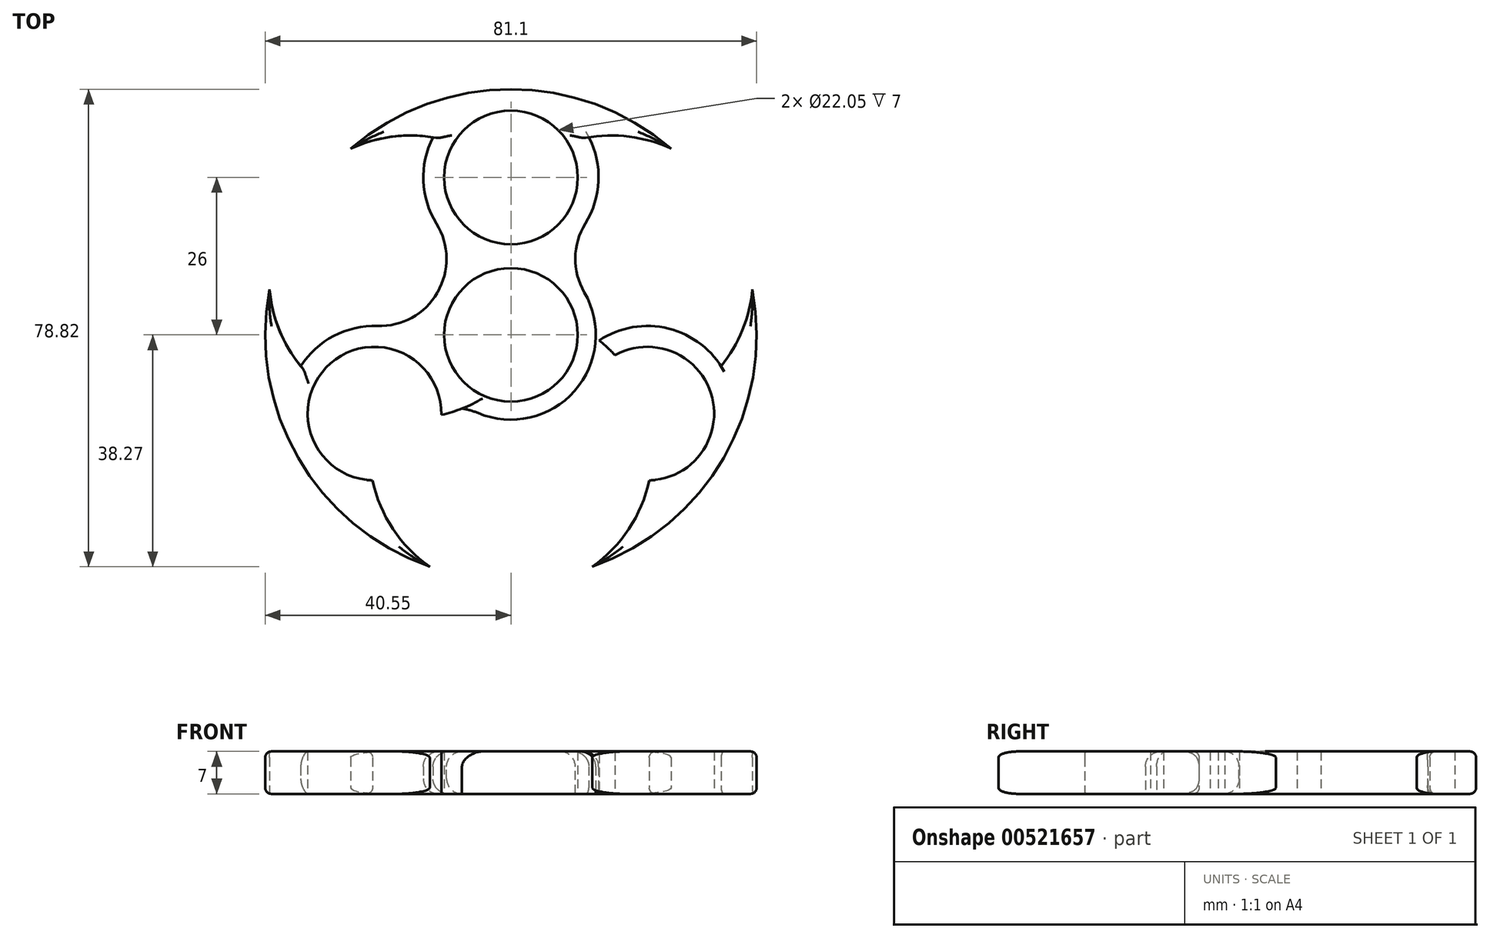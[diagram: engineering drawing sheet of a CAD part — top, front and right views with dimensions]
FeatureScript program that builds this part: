
annotation { "Feature Type Name" : "Feature", "Feature Type Description" : "" }
export const myFeature = defineFeature(function(context is Context, id is Id, definition is map)
    precondition{}
    {
        {
            var Q0;
            Q0=qCreatedBy(makeId("Top.planeOp"),FACE);
            var sketch = newSketch(context, id + "F0", { "sketchPlane" : qUnion([Q0])});
            skCircle(sketch, "E0", {"center": v(0, 0) * mm, "radius": 11.03 * mm});
            skCircle(sketch, "E1", {"center": v(0, 26) * mm, "radius": 11.03 * mm});
            skCircle(sketch, "E2.1.0", {"center": v(-22.52, -13) * mm, "radius": 11.03 * mm});
            skCircle(sketch, "E2.2.0", {"center": v(22.52, -13) * mm, "radius": 11.03 * mm});
            skCircle(sketch, "E3", {"center": v(0, 0) * mm, "radius": 40.55 * mm});
            skCircle(sketch, "E4", {"center": v(0, 0) * mm, "radius": 37 * mm});
            skCircle(sketch, "E5", {"center": v(0, 26) * mm, "radius": 14.47 * mm});
            skCircle(sketch, "E6.1.0", {"center": v(-22.52, -13) * mm, "radius": 14.47 * mm});
            skCircle(sketch, "E6.2.0", {"center": v(22.52, -13) * mm, "radius": 14.47 * mm});
            skLineSegment(sketch, "E7", {"start": v(-22.52, -13) * mm, "end": v(0, 26) * mm, "construction": true});
            skLineSegment(sketch, "E8", {"start": v(0, 26) * mm, "end": v(22.52, -13) * mm, "construction": true});
            skLineSegment(sketch, "E9", {"start": v(-22.52, -13) * mm, "end": v(22.52, -13) * mm, "construction": true});
            skPoint(sketch, "E10.endSnap0", {"position": v(0, -13) * mm});
            skCircle(sketch, "E11", {"center": v(0, 0) * mm, "radius": 42.5 * mm, "construction": true});
            skLineSegment(sketch, "E12", {"start": v(-11.26, 6.5) * mm, "end": v(-36.8, 21.25) * mm, "construction": true});
            skLineSegment(sketch, "E13", {"start": v(11.26, 6.5) * mm, "end": v(36.8, 21.25) * mm, "construction": true});
            skLineSegment(sketch, "E14", {"start": v(0, -13) * mm, "end": v(0, -42.5) * mm, "construction": true});
            skCircle(sketch, "E15", {"center": v(-16.6, 9.58) * mm, "radius": 23.34 * mm});
            skCircle(sketch, "E16", {"center": v(16.6, 9.58) * mm, "radius": 23.34 * mm});
            skCircle(sketch, "E17", {"center": v(0, -19.16) * mm, "radius": 23.34 * mm});
            skCircle(sketch, "E18", {"center": v(0, 0) * mm, "radius": 14 * mm});
            skSolve(sketch);
        }
        {
            var Q0;
            {var subQ6=sQuery(id+"F0.wireOp",EDGE,"E3");var subQ8=sQuery(id+"F0.wireOp",EDGE,"E16");var subQ10=makeQuery(id+"F0.imprint","INTERSECT",VERTEX,{"disambiguationData":[OD(0.0)],"derivedFrom":[subQ6,subQ8]});Q0=makeQuery(id+"F0.imprint","IMPRINT",FACE,{"disambiguationData":[TD([[makeQuery(id+"F0.imprint","IMPRINT",EDGE,{"disambiguationData":[TD([[subQ10,-1.0]])],"derivedFrom":subQ6}),1.0]])]});}
            var Q1;
            {var subQ0=sQuery(id+"F0.wireOp",EDGE,"E4");var subQ1=sQuery(id+"F0.wireOp",EDGE,"E1");var subQ2=makeQuery(id+"F0.imprint","INTERSECT",VERTEX,{"disambiguationData":[OD(0.0)],"derivedFrom":[subQ1,subQ0]});Q1=makeQuery(id+"F0.imprint","IMPRINT",FACE,{"disambiguationData":[TD([[makeQuery(id+"F0.imprint","IMPRINT",EDGE,{"disambiguationData":[TD([[subQ2,-1.0]])],"derivedFrom":subQ1}),-1.0]])]});}
            var Q2;
            {var subQ0=sQuery(id+"F0.wireOp",EDGE,"E5");var subQ1=sQuery(id+"F0.wireOp",EDGE,"E4");var subQ2=makeQuery(id+"F0.imprint","INTERSECT",VERTEX,{"disambiguationData":[OD(1.0)],"derivedFrom":[subQ1,subQ0]});Q2=makeQuery(id+"F0.imprint","IMPRINT",FACE,{"disambiguationData":[TD([[makeQuery(id+"F0.imprint","IMPRINT",EDGE,{"disambiguationData":[TD([[subQ2,-1.0]])],"derivedFrom":subQ1}),1.0]])]});}
            var Q3;
            {var subQ0=sQuery(id+"F0.wireOp",EDGE,"E4");var subQ1=sQuery(id+"F0.wireOp",EDGE,"E1");var subQ2=makeQuery(id+"F0.imprint","INTERSECT",VERTEX,{"disambiguationData":[OD(1.0)],"derivedFrom":[subQ1,subQ0]});Q3=makeQuery(id+"F0.imprint","IMPRINT",FACE,{"disambiguationData":[TD([[makeQuery(id+"F0.imprint","IMPRINT",EDGE,{"disambiguationData":[TD([[subQ2,-1.0]])],"derivedFrom":subQ1}),-1.0]])]});}
            var Q4;
            {var subQ0=sQuery(id+"F0.wireOp",EDGE,"E15");var subQ1=sQuery(id+"F0.wireOp",EDGE,"E1");var subQ2=makeQuery(id+"F0.imprint","INTERSECT",VERTEX,{"disambiguationData":[OD(0.0)],"derivedFrom":[subQ1,subQ0]});Q4=makeQuery(id+"F0.imprint","IMPRINT",FACE,{"disambiguationData":[TD([[makeQuery(id+"F0.imprint","IMPRINT",EDGE,{"disambiguationData":[TD([[subQ2,-1.0]])],"derivedFrom":subQ1}),-1.0]])]});}
            var Q5;
            {var subQ0=sQuery(id+"F0.wireOp",EDGE,"E4");var subQ1=sQuery(id+"F0.wireOp",EDGE,"E1");var subQ2=makeQuery(id+"F0.imprint","INTERSECT",VERTEX,{"disambiguationData":[OD(0.0)],"derivedFrom":[subQ1,subQ0]});Q5=makeQuery(id+"F0.imprint","IMPRINT",FACE,{"disambiguationData":[TD([[makeQuery(id+"F0.imprint","IMPRINT",EDGE,{"disambiguationData":[TD([[subQ2,1.0]])],"derivedFrom":subQ1}),-1.0]])]});}
            var Q6;
            {var subQ0=sQuery(id+"F0.wireOp",EDGE,"E5");var subQ1=sQuery(id+"F0.wireOp",EDGE,"E4");var subQ2=makeQuery(id+"F0.imprint","INTERSECT",VERTEX,{"disambiguationData":[OD(0.0)],"derivedFrom":[subQ1,subQ0]});Q6=makeQuery(id+"F0.imprint","IMPRINT",FACE,{"disambiguationData":[TD([[makeQuery(id+"F0.imprint","IMPRINT",EDGE,{"disambiguationData":[TD([[subQ2,1.0]])],"derivedFrom":subQ1}),1.0]])]});}
            var Q7;
            {var subQ0=sQuery(id+"F0.wireOp",EDGE,"E16");var subQ1=sQuery(id+"F0.wireOp",EDGE,"E1");var subQ2=makeQuery(id+"F0.imprint","INTERSECT",VERTEX,{"disambiguationData":[OD(0.0)],"derivedFrom":[subQ1,subQ0]});Q7=makeQuery(id+"F0.imprint","IMPRINT",FACE,{"disambiguationData":[TD([[makeQuery(id+"F0.imprint","IMPRINT",EDGE,{"disambiguationData":[TD([[subQ2,1.0]])],"derivedFrom":subQ1}),-1.0]])]});}
            var Q8;
            {var subQ0=sQuery(id+"F0.wireOp",EDGE,"E16");var subQ1=sQuery(id+"F0.wireOp",EDGE,"E2.2.0");var subQ2=makeQuery(id+"F0.imprint","INTERSECT",VERTEX,{"disambiguationData":[OD(0.0)],"derivedFrom":[subQ1,subQ0]});Q8=makeQuery(id+"F0.imprint","IMPRINT",FACE,{"disambiguationData":[TD([[makeQuery(id+"F0.imprint","IMPRINT",EDGE,{"disambiguationData":[TD([[subQ2,-1.0]])],"derivedFrom":subQ1}),-1.0]])]});}
            var Q9;
            {var subQ0=sQuery(id+"F0.wireOp",EDGE,"E4");var subQ1=sQuery(id+"F0.wireOp",EDGE,"E2.2.0");var subQ2=makeQuery(id+"F0.imprint","INTERSECT",VERTEX,{"disambiguationData":[OD(1.0)],"derivedFrom":[subQ1,subQ0]});Q9=makeQuery(id+"F0.imprint","IMPRINT",FACE,{"disambiguationData":[TD([[makeQuery(id+"F0.imprint","IMPRINT",EDGE,{"disambiguationData":[TD([[subQ2,-1.0]])],"derivedFrom":subQ1}),-1.0]])]});}
            var Q10;
            {var subQ0=sQuery(id+"F0.wireOp",EDGE,"E4");var subQ1=sQuery(id+"F0.wireOp",EDGE,"E2.2.0");var subQ2=makeQuery(id+"F0.imprint","INTERSECT",VERTEX,{"disambiguationData":[OD(0.0)],"derivedFrom":[subQ1,subQ0]});Q10=makeQuery(id+"F0.imprint","IMPRINT",FACE,{"disambiguationData":[TD([[makeQuery(id+"F0.imprint","IMPRINT",EDGE,{"disambiguationData":[TD([[subQ2,-1.0]])],"derivedFrom":subQ1}),-1.0]])]});}
            var Q11;
            {var subQ4=sQuery(id+"F0.wireOp",EDGE,"E16");var subQ8=sQuery(id+"F0.wireOp",EDGE,"E3");var subQ9=makeQuery(id+"F0.imprint","INTERSECT",VERTEX,{"disambiguationData":[OD(1.0)],"derivedFrom":[subQ8,subQ4]});Q11=makeQuery(id+"F0.imprint","IMPRINT",FACE,{"disambiguationData":[TD([[makeQuery(id+"F0.imprint","IMPRINT",EDGE,{"disambiguationData":[TD([[subQ9,1.0]])],"derivedFrom":subQ8}),1.0]])]});}
            var Q12;
            {var subQ0=sQuery(id+"F0.wireOp",EDGE,"E6.2.0");var subQ1=sQuery(id+"F0.wireOp",EDGE,"E4");var subQ2=makeQuery(id+"F0.imprint","INTERSECT",VERTEX,{"disambiguationData":[OD(1.0)],"derivedFrom":[subQ1,subQ0]});Q12=makeQuery(id+"F0.imprint","IMPRINT",FACE,{"disambiguationData":[TD([[makeQuery(id+"F0.imprint","IMPRINT",EDGE,{"disambiguationData":[TD([[subQ2,-1.0]])],"derivedFrom":subQ1}),1.0]])]});}
            var Q13;
            {var subQ0=sQuery(id+"F0.wireOp",EDGE,"E17");var subQ1=sQuery(id+"F0.wireOp",EDGE,"E4");var subQ2=makeQuery(id+"F0.imprint","INTERSECT",VERTEX,{"disambiguationData":[OD(1.0)],"derivedFrom":[subQ1,subQ0]});Q13=makeQuery(id+"F0.imprint","IMPRINT",FACE,{"disambiguationData":[TD([[makeQuery(id+"F0.imprint","IMPRINT",EDGE,{"disambiguationData":[TD([[subQ2,-1.0]])],"derivedFrom":subQ1}),1.0]])]});}
            var Q14;
            {var subQ5=sQuery(id+"F0.wireOp",EDGE,"E15");var subQ8=sQuery(id+"F0.wireOp",EDGE,"E3");var subQ9=makeQuery(id+"F0.imprint","INTERSECT",VERTEX,{"disambiguationData":[OD(1.0)],"derivedFrom":[subQ8,subQ5]});Q14=makeQuery(id+"F0.imprint","IMPRINT",FACE,{"disambiguationData":[TD([[makeQuery(id+"F0.imprint","IMPRINT",EDGE,{"disambiguationData":[TD([[subQ9,-1.0]])],"derivedFrom":subQ8}),1.0]])]});}
            var Q15;
            {var subQ0=sQuery(id+"F0.wireOp",EDGE,"E4");var subQ1=sQuery(id+"F0.wireOp",EDGE,"E2.1.0");var subQ2=makeQuery(id+"F0.imprint","INTERSECT",VERTEX,{"disambiguationData":[OD(0.0)],"derivedFrom":[subQ1,subQ0]});Q15=makeQuery(id+"F0.imprint","IMPRINT",FACE,{"disambiguationData":[TD([[makeQuery(id+"F0.imprint","IMPRINT",EDGE,{"disambiguationData":[TD([[subQ2,-1.0]])],"derivedFrom":subQ1}),-1.0]])]});}
            var Q16;
            {var subQ0=sQuery(id+"F0.wireOp",EDGE,"E15");var subQ1=sQuery(id+"F0.wireOp",EDGE,"E4");var subQ2=makeQuery(id+"F0.imprint","INTERSECT",VERTEX,{"disambiguationData":[OD(1.0)],"derivedFrom":[subQ1,subQ0]});Q16=makeQuery(id+"F0.imprint","IMPRINT",FACE,{"disambiguationData":[TD([[makeQuery(id+"F0.imprint","IMPRINT",EDGE,{"disambiguationData":[TD([[subQ2,-1.0]])],"derivedFrom":subQ1}),1.0]])]});}
            var Q17;
            {var subQ0=sQuery(id+"F0.wireOp",EDGE,"E4");var subQ1=sQuery(id+"F0.wireOp",EDGE,"E2.1.0");var subQ2=makeQuery(id+"F0.imprint","INTERSECT",VERTEX,{"disambiguationData":[OD(0.0)],"derivedFrom":[subQ1,subQ0]});Q17=makeQuery(id+"F0.imprint","IMPRINT",FACE,{"disambiguationData":[TD([[makeQuery(id+"F0.imprint","IMPRINT",EDGE,{"disambiguationData":[TD([[subQ2,1.0]])],"derivedFrom":subQ1}),-1.0]])]});}
            var Q18;
            {var subQ0=sQuery(id+"F0.wireOp",EDGE,"E4");var subQ1=sQuery(id+"F0.wireOp",EDGE,"E2.1.0");var subQ2=makeQuery(id+"F0.imprint","INTERSECT",VERTEX,{"disambiguationData":[OD(1.0)],"derivedFrom":[subQ1,subQ0]});Q18=makeQuery(id+"F0.imprint","IMPRINT",FACE,{"disambiguationData":[TD([[makeQuery(id+"F0.imprint","IMPRINT",EDGE,{"disambiguationData":[TD([[subQ2,-1.0]])],"derivedFrom":subQ1}),-1.0]])]});}
            var Q19;
            {var subQ0=sQuery(id+"F0.wireOp",EDGE,"E6.1.0");var subQ1=sQuery(id+"F0.wireOp",EDGE,"E4");var subQ2=makeQuery(id+"F0.imprint","INTERSECT",VERTEX,{"disambiguationData":[OD(1.0)],"derivedFrom":[subQ1,subQ0]});Q19=makeQuery(id+"F0.imprint","IMPRINT",FACE,{"disambiguationData":[TD([[makeQuery(id+"F0.imprint","IMPRINT",EDGE,{"disambiguationData":[TD([[subQ2,-1.0]])],"derivedFrom":subQ1}),1.0]])]});}
            var Q20;
            {var subQ0=sQuery(id+"F0.wireOp",EDGE,"E17");var subQ1=sQuery(id+"F0.wireOp",EDGE,"E2.1.0");var subQ2=makeQuery(id+"F0.imprint","INTERSECT",VERTEX,{"disambiguationData":[OD(0.0)],"derivedFrom":[subQ1,subQ0]});Q20=makeQuery(id+"F0.imprint","IMPRINT",FACE,{"disambiguationData":[TD([[makeQuery(id+"F0.imprint","IMPRINT",EDGE,{"disambiguationData":[TD([[subQ2,-1.0]])],"derivedFrom":subQ1}),-1.0]])]});}
            var Q21;
            {var subQ0=sQuery(id+"F0.wireOp",EDGE,"E15");var subQ1=sQuery(id+"F0.wireOp",EDGE,"E2.1.0");var subQ2=makeQuery(id+"F0.imprint","INTERSECT",VERTEX,{"disambiguationData":[OD(0.0)],"derivedFrom":[subQ1,subQ0]});Q21=makeQuery(id+"F0.imprint","IMPRINT",FACE,{"disambiguationData":[TD([[makeQuery(id+"F0.imprint","IMPRINT",EDGE,{"disambiguationData":[TD([[subQ2,1.0]])],"derivedFrom":subQ1}),-1.0]])]});}
            var Q22;
            {var subQ0=sQuery(id+"F0.wireOp",EDGE,"E16");var subQ1=sQuery(id+"F0.wireOp",EDGE,"E0");var subQ2=makeQuery(id+"F0.imprint","INTERSECT",VERTEX,{"disambiguationData":[OD(0.0)],"derivedFrom":[subQ1,subQ0]});Q22=makeQuery(id+"F0.imprint","IMPRINT",FACE,{"disambiguationData":[TD([[makeQuery(id+"F0.imprint","IMPRINT",EDGE,{"disambiguationData":[TD([[subQ2,-1.0]])],"derivedFrom":subQ1}),-1.0]])]});}
            var Q23;
            {var subQ1=sQuery(id+"F0.wireOp",EDGE,"E1");var subQ7=sQuery(id+"F0.wireOp",EDGE,"E16");var subQ8=makeQuery(id+"F0.imprint","INTERSECT",VERTEX,{"disambiguationData":[OD(1.0)],"derivedFrom":[subQ1,subQ7]});Q23=makeQuery(id+"F0.imprint","IMPRINT",FACE,{"disambiguationData":[TD([[makeQuery(id+"F0.imprint","IMPRINT",EDGE,{"disambiguationData":[TD([[subQ8,-1.0]])],"derivedFrom":subQ1}),-1.0]])]});}
            var Q24;
            {var subQ0=sQuery(id+"F0.wireOp",EDGE,"E18");var subQ1=sQuery(id+"F0.wireOp",EDGE,"E5");var subQ2=makeQuery(id+"F0.imprint","INTERSECT",VERTEX,{"disambiguationData":[OD(0.0)],"derivedFrom":[subQ1,subQ0]});Q24=makeQuery(id+"F0.imprint","IMPRINT",FACE,{"disambiguationData":[TD([[makeQuery(id+"F0.imprint","IMPRINT",EDGE,{"disambiguationData":[TD([[subQ2,-1.0]])],"derivedFrom":subQ1}),1.0]])]});}
            var Q25;
            {var subQ1=sQuery(id+"F0.wireOp",EDGE,"E0");var subQ7=sQuery(id+"F0.wireOp",EDGE,"E15");var subQ10=makeQuery(id+"F0.imprint","INTERSECT",VERTEX,{"disambiguationData":[OD(0.0)],"derivedFrom":[subQ1,subQ7]});Q25=makeQuery(id+"F0.imprint","IMPRINT",FACE,{"disambiguationData":[TD([[makeQuery(id+"F0.imprint","IMPRINT",EDGE,{"disambiguationData":[TD([[subQ10,-1.0]])],"derivedFrom":subQ1}),-1.0]])]});}
            var Q26;
            {var subQ0=sQuery(id+"F0.wireOp",EDGE,"E15");var subQ1=sQuery(id+"F0.wireOp",EDGE,"E0");var subQ2=makeQuery(id+"F0.imprint","INTERSECT",VERTEX,{"disambiguationData":[OD(0.0)],"derivedFrom":[subQ1,subQ0]});Q26=makeQuery(id+"F0.imprint","IMPRINT",FACE,{"disambiguationData":[TD([[makeQuery(id+"F0.imprint","IMPRINT",EDGE,{"disambiguationData":[TD([[subQ2,1.0]])],"derivedFrom":subQ1}),-1.0]])]});}
            var Q27;
            {var subQ1=sQuery(id+"F0.wireOp",EDGE,"E0");var subQ8=sQuery(id+"F0.wireOp",EDGE,"E17");var subQ9=makeQuery(id+"F0.imprint","INTERSECT",VERTEX,{"disambiguationData":[OD(0.0)],"derivedFrom":[subQ1,subQ8]});Q27=makeQuery(id+"F0.imprint","IMPRINT",FACE,{"disambiguationData":[TD([[makeQuery(id+"F0.imprint","IMPRINT",EDGE,{"disambiguationData":[TD([[subQ9,1.0]])],"derivedFrom":subQ1}),-1.0]])]});}
            var Q28;
            {var subQ0=sQuery(id+"F0.wireOp",EDGE,"E18");var subQ1=sQuery(id+"F0.wireOp",EDGE,"E6.2.0");var subQ2=makeQuery(id+"F0.imprint","INTERSECT",VERTEX,{"disambiguationData":[OD(0.0)],"derivedFrom":[subQ1,subQ0]});Q28=makeQuery(id+"F0.imprint","IMPRINT",FACE,{"disambiguationData":[TD([[makeQuery(id+"F0.imprint","IMPRINT",EDGE,{"disambiguationData":[TD([[subQ2,-1.0]])],"derivedFrom":subQ1}),1.0]])]});}
            var Q29;
            {var subQ1=sQuery(id+"F0.wireOp",EDGE,"E2.2.0");var subQ7=sQuery(id+"F0.wireOp",EDGE,"E17");var subQ10=makeQuery(id+"F0.imprint","INTERSECT",VERTEX,{"disambiguationData":[OD(1.0)],"derivedFrom":[subQ1,subQ7]});Q29=makeQuery(id+"F0.imprint","IMPRINT",FACE,{"disambiguationData":[TD([[makeQuery(id+"F0.imprint","IMPRINT",EDGE,{"disambiguationData":[TD([[subQ10,-1.0]])],"derivedFrom":subQ1}),-1.0]])]});}
            var Q30;
            {var subQ0=sQuery(id+"F0.wireOp",EDGE,"E4");var subQ1=sQuery(id+"F0.wireOp",EDGE,"E2.2.0");var subQ2=makeQuery(id+"F0.imprint","INTERSECT",VERTEX,{"disambiguationData":[OD(0.0)],"derivedFrom":[subQ1,subQ0]});Q30=makeQuery(id+"F0.imprint","IMPRINT",FACE,{"disambiguationData":[TD([[makeQuery(id+"F0.imprint","IMPRINT",EDGE,{"disambiguationData":[TD([[subQ2,1.0]])],"derivedFrom":subQ1}),-1.0]])]});}
            var Q31;
            {var subQ0=sQuery(id+"F0.wireOp",EDGE,"E17");var subQ1=sQuery(id+"F0.wireOp",EDGE,"E2.2.0");var subQ2=makeQuery(id+"F0.imprint","INTERSECT",VERTEX,{"disambiguationData":[OD(0.0)],"derivedFrom":[subQ1,subQ0]});Q31=makeQuery(id+"F0.imprint","IMPRINT",FACE,{"disambiguationData":[TD([[makeQuery(id+"F0.imprint","IMPRINT",EDGE,{"disambiguationData":[TD([[subQ2,1.0]])],"derivedFrom":subQ1}),-1.0]])]});}
            var Q32;
            {var subQ0=sQuery(id+"F0.wireOp",EDGE,"E15");var subQ1=sQuery(id+"F0.wireOp",EDGE,"E0");var subQ2=makeQuery(id+"F0.imprint","INTERSECT",VERTEX,{"disambiguationData":[OD(1.0)],"derivedFrom":[subQ1,subQ0]});Q32=makeQuery(id+"F0.imprint","IMPRINT",FACE,{"disambiguationData":[TD([[makeQuery(id+"F0.imprint","IMPRINT",EDGE,{"disambiguationData":[TD([[subQ2,-1.0]])],"derivedFrom":subQ1}),-1.0]])]});}
            var Q33;
            {var subQ0=sQuery(id+"F0.wireOp",EDGE,"E17");var subQ1=sQuery(id+"F0.wireOp",EDGE,"E0");var subQ2=makeQuery(id+"F0.imprint","INTERSECT",VERTEX,{"disambiguationData":[OD(1.0)],"derivedFrom":[subQ1,subQ0]});Q33=makeQuery(id+"F0.imprint","IMPRINT",FACE,{"disambiguationData":[TD([[makeQuery(id+"F0.imprint","IMPRINT",EDGE,{"disambiguationData":[TD([[subQ2,-1.0]])],"derivedFrom":subQ1}),-1.0]])]});}
            var Q34;
            {var subQ5=sQuery(id+"F0.wireOp",EDGE,"E15");var subQ6=sQuery(id+"F0.wireOp",EDGE,"E2.1.0");var subQ7=makeQuery(id+"F0.imprint","INTERSECT",VERTEX,{"disambiguationData":[OD(1.0)],"derivedFrom":[subQ6,subQ5]});Q34=makeQuery(id+"F0.imprint","IMPRINT",FACE,{"disambiguationData":[TD([[makeQuery(id+"F0.imprint","IMPRINT",EDGE,{"disambiguationData":[TD([[subQ7,-1.0]])],"derivedFrom":subQ6}),-1.0]])]});}
            var Q35;
            {var subQ0=sQuery(id+"F0.wireOp",EDGE,"E18");var subQ1=sQuery(id+"F0.wireOp",EDGE,"E6.1.0");var subQ2=makeQuery(id+"F0.imprint","INTERSECT",VERTEX,{"disambiguationData":[OD(0.0)],"derivedFrom":[subQ1,subQ0]});Q35=makeQuery(id+"F0.imprint","IMPRINT",FACE,{"disambiguationData":[TD([[makeQuery(id+"F0.imprint","IMPRINT",EDGE,{"disambiguationData":[TD([[subQ2,-1.0]])],"derivedFrom":subQ1}),1.0]])]});}
            extrude(context, id + "F1", {"entities" : qUnion([Q0, Q1, Q2, Q3, Q4, Q5, Q6, Q7, Q8, Q9, Q10, Q11, Q12, Q13, Q14, Q15, Q16, Q17, Q18, Q19, Q20, Q21, Q22, Q23, Q24, Q25, Q26, Q27, Q28, Q29, Q30, Q31, Q32, Q33, Q34, Q35]), "depth" : 7 * mm, "offsetDistance" : 25 * mm});
        }
        {
            var Q0;
            {var subQ0=sQuery(id+"F0.wireOp",EDGE,"E18");var subQ1=sQuery(id+"F0.wireOp",EDGE,"E5");Q0=makeQuery(id+"F1.opExtrude","SWEPT_EDGE",EDGE,{"disambiguationData":[OSD([subQ1,subQ0]),TDD([makeQuery(id+"F0.imprint","INTERSECT",VERTEX,{"disambiguationData":[OD(1.0)],"derivedFrom":[subQ1,subQ0]})])]});}
            var Q1;
            {var subQ0=sQuery(id+"F0.wireOp",EDGE,"E18");var subQ1=sQuery(id+"F0.wireOp",EDGE,"E6.2.0");Q1=makeQuery(id+"F1.opExtrude","SWEPT_EDGE",EDGE,{"disambiguationData":[OSD([subQ1,subQ0]),TDD([makeQuery(id+"F0.imprint","INTERSECT",VERTEX,{"disambiguationData":[OD(0.0)],"derivedFrom":[subQ1,subQ0]})])]});}
            var Q2;
            {var subQ0=sQuery(id+"F0.wireOp",EDGE,"E18");var subQ1=sQuery(id+"F0.wireOp",EDGE,"E6.2.0");Q2=makeQuery(id+"F1.opExtrude","SWEPT_EDGE",EDGE,{"disambiguationData":[OSD([subQ1,subQ0]),TDD([makeQuery(id+"F0.imprint","INTERSECT",VERTEX,{"disambiguationData":[OD(1.0)],"derivedFrom":[subQ1,subQ0]})])]});}
            var Q3;
            {var subQ0=sQuery(id+"F0.wireOp",EDGE,"E18");var subQ1=sQuery(id+"F0.wireOp",EDGE,"E6.1.0");Q3=makeQuery(id+"F1.opExtrude","SWEPT_EDGE",EDGE,{"disambiguationData":[OSD([subQ1,subQ0]),TDD([makeQuery(id+"F0.imprint","INTERSECT",VERTEX,{"disambiguationData":[OD(0.0)],"derivedFrom":[subQ1,subQ0]})])]});}
            var Q4;
            {var subQ0=sQuery(id+"F0.wireOp",EDGE,"E18");var subQ1=sQuery(id+"F0.wireOp",EDGE,"E6.1.0");Q4=makeQuery(id+"F1.opExtrude","SWEPT_EDGE",EDGE,{"disambiguationData":[OSD([subQ1,subQ0]),TDD([makeQuery(id+"F0.imprint","INTERSECT",VERTEX,{"disambiguationData":[OD(1.0)],"derivedFrom":[subQ1,subQ0]})])]});}
            var Q5;
            {var subQ0=sQuery(id+"F0.wireOp",EDGE,"E18");var subQ1=sQuery(id+"F0.wireOp",EDGE,"E5");Q5=makeQuery(id+"F1.opExtrude","SWEPT_EDGE",EDGE,{"disambiguationData":[OSD([subQ1,subQ0]),TDD([makeQuery(id+"F0.imprint","INTERSECT",VERTEX,{"disambiguationData":[OD(0.0)],"derivedFrom":[subQ1,subQ0]})])]});}
            fillet(context, id + "F2", {"entities" : qUnion([Q0, Q1, Q2, Q3, Q4, Q5]), "radius" : 11 * mm, "tangentPropagation" : true, "allowEdgeOverflow" : false});
        }
        {
            var Q0;
            {var subQ0=sQuery(id+"F0.wireOp",EDGE,"E5");var subQ1=makeQuery(id+"F0.imprint","INTERSECT",VERTEX,{"disambiguationData":[OD(1.0)],"derivedFrom":[subQ0,sQuery(id+"F0.wireOp",EDGE,"E16")]});Q0=makeQuery(id+"F1.opExtrude","CAP_EDGE",EDGE,{"disambiguationData":[OSD([subQ0]),TDD([makeQuery(id+"F0.imprint","IMPRINT",EDGE,{"disambiguationData":[TD([[makeQuery(id+"F0.imprint","INTERSECT",VERTEX,{"disambiguationData":[OD(0.0)],"derivedFrom":[subQ0,sQuery(id+"F0.wireOp",EDGE,"E15")]}),-1.0]])],"derivedFrom":subQ0}),makeQuery(id+"F0.imprint","IMPRINT",EDGE,{"disambiguationData":[TD([[subQ1,-1.0]])],"derivedFrom":subQ0})])],"isStart":false});}
            var Q1;
            {var subQ0=sQuery(id+"F0.wireOp",EDGE,"E18");var subQ1=sQuery(id+"F0.wireOp",EDGE,"E5");Q1=makeQuery(id+"F2.opFillet","BLEND_EDGE",EDGE,{"blendedFrom":[makeQuery(id+"F1.opExtrude","SWEPT_EDGE",EDGE,{"disambiguationData":[OSD([subQ1,subQ0]),TDD([makeQuery(id+"F0.imprint","INTERSECT",VERTEX,{"disambiguationData":[OD(1.0)],"derivedFrom":[subQ1,subQ0]})])]}),makeQuery(id+"F1.opExtrude","CAP_FACE",FACE,{"disambiguationData":[OSD([sQuery(id+"F0.wireOp",EDGE,"E0"),sQuery(id+"F0.wireOp",EDGE,"E1"),sQuery(id+"F0.wireOp",EDGE,"E2.1.0"),sQuery(id+"F0.wireOp",EDGE,"E2.2.0"),sQuery(id+"F0.wireOp",EDGE,"E3"),subQ1,sQuery(id+"F0.wireOp",EDGE,"E6.1.0"),sQuery(id+"F0.wireOp",EDGE,"E6.2.0"),sQuery(id+"F0.wireOp",EDGE,"E15"),sQuery(id+"F0.wireOp",EDGE,"E16"),sQuery(id+"F0.wireOp",EDGE,"E17"),subQ0])],"isStart":false})],"blendedInto":[makeQuery(id+"F1.opExtrude","CAP_FACE",FACE,{"disambiguationData":[OSD([sQuery(id+"F0.wireOp",EDGE,"E0"),sQuery(id+"F0.wireOp",EDGE,"E1"),sQuery(id+"F0.wireOp",EDGE,"E2.1.0"),sQuery(id+"F0.wireOp",EDGE,"E2.2.0"),sQuery(id+"F0.wireOp",EDGE,"E3"),subQ1,sQuery(id+"F0.wireOp",EDGE,"E6.1.0"),sQuery(id+"F0.wireOp",EDGE,"E6.2.0"),sQuery(id+"F0.wireOp",EDGE,"E15"),sQuery(id+"F0.wireOp",EDGE,"E16"),sQuery(id+"F0.wireOp",EDGE,"E17"),subQ0])],"isStart":false})]});}
            var Q2;
            {var subQ0=sQuery(id+"F0.wireOp",EDGE,"E18");var subQ1=sQuery(id+"F0.wireOp",EDGE,"E6.2.0");Q2=makeQuery(id+"F2.opFillet","BLEND_EDGE",EDGE,{"blendedFrom":[makeQuery(id+"F1.opExtrude","SWEPT_EDGE",EDGE,{"disambiguationData":[OSD([subQ1,subQ0]),TDD([makeQuery(id+"F0.imprint","INTERSECT",VERTEX,{"disambiguationData":[OD(1.0)],"derivedFrom":[subQ1,subQ0]})])]}),makeQuery(id+"F1.opExtrude","CAP_FACE",FACE,{"disambiguationData":[OSD([sQuery(id+"F0.wireOp",EDGE,"E0"),sQuery(id+"F0.wireOp",EDGE,"E1"),sQuery(id+"F0.wireOp",EDGE,"E2.1.0"),sQuery(id+"F0.wireOp",EDGE,"E2.2.0"),sQuery(id+"F0.wireOp",EDGE,"E3"),sQuery(id+"F0.wireOp",EDGE,"E5"),sQuery(id+"F0.wireOp",EDGE,"E6.1.0"),subQ1,sQuery(id+"F0.wireOp",EDGE,"E15"),sQuery(id+"F0.wireOp",EDGE,"E16"),sQuery(id+"F0.wireOp",EDGE,"E17"),subQ0])],"isStart":false})],"blendedInto":[makeQuery(id+"F1.opExtrude","CAP_FACE",FACE,{"disambiguationData":[OSD([sQuery(id+"F0.wireOp",EDGE,"E0"),sQuery(id+"F0.wireOp",EDGE,"E1"),sQuery(id+"F0.wireOp",EDGE,"E2.1.0"),sQuery(id+"F0.wireOp",EDGE,"E2.2.0"),sQuery(id+"F0.wireOp",EDGE,"E3"),sQuery(id+"F0.wireOp",EDGE,"E5"),sQuery(id+"F0.wireOp",EDGE,"E6.1.0"),subQ1,sQuery(id+"F0.wireOp",EDGE,"E15"),sQuery(id+"F0.wireOp",EDGE,"E16"),sQuery(id+"F0.wireOp",EDGE,"E17"),subQ0])],"isStart":false})]});}
            var Q3;
            {var subQ0=sQuery(id+"F0.wireOp",EDGE,"E18");var subQ1=sQuery(id+"F0.wireOp",EDGE,"E6.2.0");Q3=makeQuery(id+"F2.opFillet","BLEND_EDGE",EDGE,{"blendedFrom":[makeQuery(id+"F1.opExtrude","SWEPT_EDGE",EDGE,{"disambiguationData":[OSD([subQ1,subQ0]),TDD([makeQuery(id+"F0.imprint","INTERSECT",VERTEX,{"disambiguationData":[OD(1.0)],"derivedFrom":[subQ1,subQ0]})])]}),makeQuery(id+"F1.opExtrude","CAP_FACE",FACE,{"disambiguationData":[OSD([sQuery(id+"F0.wireOp",EDGE,"E0"),sQuery(id+"F0.wireOp",EDGE,"E1"),sQuery(id+"F0.wireOp",EDGE,"E2.1.0"),sQuery(id+"F0.wireOp",EDGE,"E2.2.0"),sQuery(id+"F0.wireOp",EDGE,"E3"),sQuery(id+"F0.wireOp",EDGE,"E5"),sQuery(id+"F0.wireOp",EDGE,"E6.1.0"),subQ1,sQuery(id+"F0.wireOp",EDGE,"E15"),sQuery(id+"F0.wireOp",EDGE,"E16"),sQuery(id+"F0.wireOp",EDGE,"E17"),subQ0])],"isStart":true})],"blendedInto":[makeQuery(id+"F1.opExtrude","CAP_FACE",FACE,{"disambiguationData":[OSD([sQuery(id+"F0.wireOp",EDGE,"E0"),sQuery(id+"F0.wireOp",EDGE,"E1"),sQuery(id+"F0.wireOp",EDGE,"E2.1.0"),sQuery(id+"F0.wireOp",EDGE,"E2.2.0"),sQuery(id+"F0.wireOp",EDGE,"E3"),sQuery(id+"F0.wireOp",EDGE,"E5"),sQuery(id+"F0.wireOp",EDGE,"E6.1.0"),subQ1,sQuery(id+"F0.wireOp",EDGE,"E15"),sQuery(id+"F0.wireOp",EDGE,"E16"),sQuery(id+"F0.wireOp",EDGE,"E17"),subQ0])],"isStart":true})]});}
            var Q4;
            {var subQ0=sQuery(id+"F0.wireOp",EDGE,"E18");var subQ1=sQuery(id+"F0.wireOp",EDGE,"E5");Q4=makeQuery(id+"F2.opFillet","BLEND_EDGE",EDGE,{"blendedFrom":[makeQuery(id+"F1.opExtrude","SWEPT_EDGE",EDGE,{"disambiguationData":[OSD([subQ1,subQ0]),TDD([makeQuery(id+"F0.imprint","INTERSECT",VERTEX,{"disambiguationData":[OD(0.0)],"derivedFrom":[subQ1,subQ0]})])]}),makeQuery(id+"F1.opExtrude","CAP_FACE",FACE,{"disambiguationData":[OSD([sQuery(id+"F0.wireOp",EDGE,"E0"),sQuery(id+"F0.wireOp",EDGE,"E1"),sQuery(id+"F0.wireOp",EDGE,"E2.1.0"),sQuery(id+"F0.wireOp",EDGE,"E2.2.0"),sQuery(id+"F0.wireOp",EDGE,"E3"),subQ1,sQuery(id+"F0.wireOp",EDGE,"E6.1.0"),sQuery(id+"F0.wireOp",EDGE,"E6.2.0"),sQuery(id+"F0.wireOp",EDGE,"E15"),sQuery(id+"F0.wireOp",EDGE,"E16"),sQuery(id+"F0.wireOp",EDGE,"E17"),subQ0])],"isStart":true})],"blendedInto":[makeQuery(id+"F1.opExtrude","CAP_FACE",FACE,{"disambiguationData":[OSD([sQuery(id+"F0.wireOp",EDGE,"E0"),sQuery(id+"F0.wireOp",EDGE,"E1"),sQuery(id+"F0.wireOp",EDGE,"E2.1.0"),sQuery(id+"F0.wireOp",EDGE,"E2.2.0"),sQuery(id+"F0.wireOp",EDGE,"E3"),subQ1,sQuery(id+"F0.wireOp",EDGE,"E6.1.0"),sQuery(id+"F0.wireOp",EDGE,"E6.2.0"),sQuery(id+"F0.wireOp",EDGE,"E15"),sQuery(id+"F0.wireOp",EDGE,"E16"),sQuery(id+"F0.wireOp",EDGE,"E17"),subQ0])],"isStart":true})]});}
            var Q5;
            {var subQ0=sQuery(id+"F0.wireOp",EDGE,"E18");var subQ1=sQuery(id+"F0.wireOp",EDGE,"E6.2.0");Q5=makeQuery(id+"F2.opFillet","BLEND_EDGE",EDGE,{"blendedFrom":[makeQuery(id+"F1.opExtrude","SWEPT_EDGE",EDGE,{"disambiguationData":[OSD([subQ1,subQ0]),TDD([makeQuery(id+"F0.imprint","INTERSECT",VERTEX,{"disambiguationData":[OD(0.0)],"derivedFrom":[subQ1,subQ0]})])]}),makeQuery(id+"F1.opExtrude","CAP_FACE",FACE,{"disambiguationData":[OSD([sQuery(id+"F0.wireOp",EDGE,"E0"),sQuery(id+"F0.wireOp",EDGE,"E1"),sQuery(id+"F0.wireOp",EDGE,"E2.1.0"),sQuery(id+"F0.wireOp",EDGE,"E2.2.0"),sQuery(id+"F0.wireOp",EDGE,"E3"),sQuery(id+"F0.wireOp",EDGE,"E5"),sQuery(id+"F0.wireOp",EDGE,"E6.1.0"),subQ1,sQuery(id+"F0.wireOp",EDGE,"E15"),sQuery(id+"F0.wireOp",EDGE,"E16"),sQuery(id+"F0.wireOp",EDGE,"E17"),subQ0])],"isStart":true})],"blendedInto":[makeQuery(id+"F1.opExtrude","CAP_FACE",FACE,{"disambiguationData":[OSD([sQuery(id+"F0.wireOp",EDGE,"E0"),sQuery(id+"F0.wireOp",EDGE,"E1"),sQuery(id+"F0.wireOp",EDGE,"E2.1.0"),sQuery(id+"F0.wireOp",EDGE,"E2.2.0"),sQuery(id+"F0.wireOp",EDGE,"E3"),sQuery(id+"F0.wireOp",EDGE,"E5"),sQuery(id+"F0.wireOp",EDGE,"E6.1.0"),subQ1,sQuery(id+"F0.wireOp",EDGE,"E15"),sQuery(id+"F0.wireOp",EDGE,"E16"),sQuery(id+"F0.wireOp",EDGE,"E17"),subQ0])],"isStart":true})]});}
            fillet(context, id + "F3", {"entities" : qUnion([Q0, Q1, Q2, Q3, Q4, Q5]), "radius" : 2.5 * mm, "tangentPropagation" : true, "allowEdgeOverflow" : false});
        }
        {
            var Q0;
            {var subQ0=sQuery(id+"F0.wireOp",EDGE,"E3");Q0=makeQuery(id+"F1.opExtrude","CAP_EDGE",EDGE,{"disambiguationData":[OSD([subQ0]),TDD([makeQuery(id+"F0.imprint","IMPRINT",EDGE,{"disambiguationData":[TD([[makeQuery(id+"F0.imprint","INTERSECT",VERTEX,{"disambiguationData":[OD(1.0)],"derivedFrom":[subQ0,sQuery(id+"F0.wireOp",EDGE,"E15")]}),-1.0]])],"derivedFrom":subQ0})])],"isStart":false});}
            var Q1;
            {var subQ0=sQuery(id+"F0.wireOp",EDGE,"E17");var subQ1=makeQuery(id+"F0.imprint","INTERSECT",VERTEX,{"disambiguationData":[OD(0.0)],"derivedFrom":[sQuery(id+"F0.wireOp",EDGE,"E4"),subQ0]});Q1=makeQuery(id+"F1.opExtrude","CAP_EDGE",EDGE,{"disambiguationData":[OSD([subQ0]),TDD([makeQuery(id+"F0.imprint","IMPRINT",EDGE,{"disambiguationData":[TD([[subQ1,1.0]])],"derivedFrom":subQ0}),makeQuery(id+"F0.imprint","IMPRINT",EDGE,{"disambiguationData":[TD([[makeQuery(id+"F0.imprint","INTERSECT",VERTEX,{"disambiguationData":[OD(0.0)],"derivedFrom":[sQuery(id+"F0.wireOp",EDGE,"E3"),subQ0]}),1.0]])],"derivedFrom":subQ0})])],"isStart":false});}
            var Q2;
            {var subQ0=sQuery(id+"F0.wireOp",EDGE,"E15");var subQ1=makeQuery(id+"F0.imprint","INTERSECT",VERTEX,{"disambiguationData":[OD(1.0)],"derivedFrom":[sQuery(id+"F0.wireOp",EDGE,"E4"),subQ0]});Q2=makeQuery(id+"F1.opExtrude","CAP_EDGE",EDGE,{"disambiguationData":[OSD([subQ0]),TDD([makeQuery(id+"F0.imprint","IMPRINT",EDGE,{"disambiguationData":[TD([[makeQuery(id+"F0.imprint","INTERSECT",VERTEX,{"disambiguationData":[OD(1.0)],"derivedFrom":[sQuery(id+"F0.wireOp",EDGE,"E3"),subQ0]}),-1.0]])],"derivedFrom":subQ0}),makeQuery(id+"F0.imprint","IMPRINT",EDGE,{"disambiguationData":[TD([[subQ1,-1.0]])],"derivedFrom":subQ0})])],"isStart":false});}
            var Q3;
            {var subQ0=sQuery(id+"F0.wireOp",EDGE,"E15");var subQ1=makeQuery(id+"F0.imprint","INTERSECT",VERTEX,{"disambiguationData":[OD(0.0)],"derivedFrom":[sQuery(id+"F0.wireOp",EDGE,"E4"),subQ0]});Q3=makeQuery(id+"F1.opExtrude","CAP_EDGE",EDGE,{"disambiguationData":[OSD([subQ0]),TDD([makeQuery(id+"F0.imprint","IMPRINT",EDGE,{"disambiguationData":[TD([[subQ1,1.0]])],"derivedFrom":subQ0}),makeQuery(id+"F0.imprint","IMPRINT",EDGE,{"disambiguationData":[TD([[makeQuery(id+"F0.imprint","INTERSECT",VERTEX,{"disambiguationData":[OD(0.0)],"derivedFrom":[sQuery(id+"F0.wireOp",EDGE,"E3"),subQ0]}),1.0]])],"derivedFrom":subQ0})])],"isStart":false});}
            var Q4;
            {var subQ0=sQuery(id+"F0.wireOp",EDGE,"E3");Q4=makeQuery(id+"F1.opExtrude","CAP_EDGE",EDGE,{"disambiguationData":[OSD([subQ0]),TDD([makeQuery(id+"F0.imprint","IMPRINT",EDGE,{"disambiguationData":[TD([[makeQuery(id+"F0.imprint","INTERSECT",VERTEX,{"disambiguationData":[OD(0.0)],"derivedFrom":[subQ0,sQuery(id+"F0.wireOp",EDGE,"E16")]}),-1.0]])],"derivedFrom":subQ0})])],"isStart":false});}
            var Q5;
            {var subQ0=sQuery(id+"F0.wireOp",EDGE,"E16");var subQ1=makeQuery(id+"F0.imprint","INTERSECT",VERTEX,{"disambiguationData":[OD(0.0)],"derivedFrom":[sQuery(id+"F0.wireOp",EDGE,"E4"),subQ0]});Q5=makeQuery(id+"F1.opExtrude","CAP_EDGE",EDGE,{"disambiguationData":[OSD([subQ0]),TDD([makeQuery(id+"F0.imprint","IMPRINT",EDGE,{"disambiguationData":[TD([[makeQuery(id+"F0.imprint","INTERSECT",VERTEX,{"disambiguationData":[OD(0.0)],"derivedFrom":[sQuery(id+"F0.wireOp",EDGE,"E3"),subQ0]}),-1.0]])],"derivedFrom":subQ0}),makeQuery(id+"F0.imprint","IMPRINT",EDGE,{"disambiguationData":[TD([[subQ1,-1.0]])],"derivedFrom":subQ0})])],"isStart":false});}
            var Q6;
            {var subQ0=sQuery(id+"F0.wireOp",EDGE,"E3");Q6=makeQuery(id+"F1.opExtrude","CAP_EDGE",EDGE,{"disambiguationData":[OSD([subQ0]),TDD([makeQuery(id+"F0.imprint","IMPRINT",EDGE,{"disambiguationData":[TD([[makeQuery(id+"F0.imprint","INTERSECT",VERTEX,{"disambiguationData":[OD(1.0)],"derivedFrom":[subQ0,sQuery(id+"F0.wireOp",EDGE,"E16")]}),1.0]])],"derivedFrom":subQ0})])],"isStart":false});}
            var Q7;
            {var subQ0=sQuery(id+"F0.wireOp",EDGE,"E17");var subQ1=makeQuery(id+"F0.imprint","INTERSECT",VERTEX,{"disambiguationData":[OD(1.0)],"derivedFrom":[sQuery(id+"F0.wireOp",EDGE,"E4"),subQ0]});Q7=makeQuery(id+"F1.opExtrude","CAP_EDGE",EDGE,{"disambiguationData":[OSD([subQ0]),TDD([makeQuery(id+"F0.imprint","IMPRINT",EDGE,{"disambiguationData":[TD([[makeQuery(id+"F0.imprint","INTERSECT",VERTEX,{"disambiguationData":[OD(1.0)],"derivedFrom":[sQuery(id+"F0.wireOp",EDGE,"E3"),subQ0]}),-1.0]])],"derivedFrom":subQ0}),makeQuery(id+"F0.imprint","IMPRINT",EDGE,{"disambiguationData":[TD([[subQ1,-1.0]])],"derivedFrom":subQ0})])],"isStart":false});}
            var Q8;
            {var subQ0=sQuery(id+"F0.wireOp",EDGE,"E16");var subQ1=makeQuery(id+"F0.imprint","INTERSECT",VERTEX,{"disambiguationData":[OD(1.0)],"derivedFrom":[sQuery(id+"F0.wireOp",EDGE,"E4"),subQ0]});Q8=makeQuery(id+"F1.opExtrude","CAP_EDGE",EDGE,{"disambiguationData":[OSD([subQ0]),TDD([makeQuery(id+"F0.imprint","IMPRINT",EDGE,{"disambiguationData":[TD([[subQ1,1.0]])],"derivedFrom":subQ0}),makeQuery(id+"F0.imprint","IMPRINT",EDGE,{"disambiguationData":[TD([[makeQuery(id+"F0.imprint","INTERSECT",VERTEX,{"disambiguationData":[OD(1.0)],"derivedFrom":[sQuery(id+"F0.wireOp",EDGE,"E3"),subQ0]}),1.0]])],"derivedFrom":subQ0})])],"isStart":false});}
            var Q9;
            {var subQ0=sQuery(id+"F0.wireOp",EDGE,"E3");Q9=makeQuery(id+"F1.opExtrude","CAP_EDGE",EDGE,{"disambiguationData":[OSD([subQ0]),TDD([makeQuery(id+"F0.imprint","IMPRINT",EDGE,{"disambiguationData":[TD([[makeQuery(id+"F0.imprint","INTERSECT",VERTEX,{"disambiguationData":[OD(1.0)],"derivedFrom":[subQ0,sQuery(id+"F0.wireOp",EDGE,"E15")]}),-1.0]])],"derivedFrom":subQ0})])],"isStart":true});}
            var Q10;
            {var subQ0=sQuery(id+"F0.wireOp",EDGE,"E17");var subQ1=makeQuery(id+"F0.imprint","INTERSECT",VERTEX,{"disambiguationData":[OD(0.0)],"derivedFrom":[sQuery(id+"F0.wireOp",EDGE,"E4"),subQ0]});Q10=makeQuery(id+"F1.opExtrude","CAP_EDGE",EDGE,{"disambiguationData":[OSD([subQ0]),TDD([makeQuery(id+"F0.imprint","IMPRINT",EDGE,{"disambiguationData":[TD([[subQ1,1.0]])],"derivedFrom":subQ0}),makeQuery(id+"F0.imprint","IMPRINT",EDGE,{"disambiguationData":[TD([[makeQuery(id+"F0.imprint","INTERSECT",VERTEX,{"disambiguationData":[OD(0.0)],"derivedFrom":[sQuery(id+"F0.wireOp",EDGE,"E3"),subQ0]}),1.0]])],"derivedFrom":subQ0})])],"isStart":true});}
            var Q11;
            {var subQ0=sQuery(id+"F0.wireOp",EDGE,"E15");var subQ1=makeQuery(id+"F0.imprint","INTERSECT",VERTEX,{"disambiguationData":[OD(1.0)],"derivedFrom":[sQuery(id+"F0.wireOp",EDGE,"E4"),subQ0]});Q11=makeQuery(id+"F1.opExtrude","CAP_EDGE",EDGE,{"disambiguationData":[OSD([subQ0]),TDD([makeQuery(id+"F0.imprint","IMPRINT",EDGE,{"disambiguationData":[TD([[makeQuery(id+"F0.imprint","INTERSECT",VERTEX,{"disambiguationData":[OD(1.0)],"derivedFrom":[sQuery(id+"F0.wireOp",EDGE,"E3"),subQ0]}),-1.0]])],"derivedFrom":subQ0}),makeQuery(id+"F0.imprint","IMPRINT",EDGE,{"disambiguationData":[TD([[subQ1,-1.0]])],"derivedFrom":subQ0})])],"isStart":true});}
            var Q12;
            {var subQ0=sQuery(id+"F0.wireOp",EDGE,"E15");var subQ1=makeQuery(id+"F0.imprint","INTERSECT",VERTEX,{"disambiguationData":[OD(0.0)],"derivedFrom":[sQuery(id+"F0.wireOp",EDGE,"E4"),subQ0]});Q12=makeQuery(id+"F1.opExtrude","CAP_EDGE",EDGE,{"disambiguationData":[OSD([subQ0]),TDD([makeQuery(id+"F0.imprint","IMPRINT",EDGE,{"disambiguationData":[TD([[subQ1,1.0]])],"derivedFrom":subQ0}),makeQuery(id+"F0.imprint","IMPRINT",EDGE,{"disambiguationData":[TD([[makeQuery(id+"F0.imprint","INTERSECT",VERTEX,{"disambiguationData":[OD(0.0)],"derivedFrom":[sQuery(id+"F0.wireOp",EDGE,"E3"),subQ0]}),1.0]])],"derivedFrom":subQ0})])],"isStart":true});}
            var Q13;
            {var subQ0=sQuery(id+"F0.wireOp",EDGE,"E3");Q13=makeQuery(id+"F1.opExtrude","CAP_EDGE",EDGE,{"disambiguationData":[OSD([subQ0]),TDD([makeQuery(id+"F0.imprint","IMPRINT",EDGE,{"disambiguationData":[TD([[makeQuery(id+"F0.imprint","INTERSECT",VERTEX,{"disambiguationData":[OD(0.0)],"derivedFrom":[subQ0,sQuery(id+"F0.wireOp",EDGE,"E16")]}),-1.0]])],"derivedFrom":subQ0})])],"isStart":true});}
            var Q14;
            {var subQ0=sQuery(id+"F0.wireOp",EDGE,"E16");var subQ1=makeQuery(id+"F0.imprint","INTERSECT",VERTEX,{"disambiguationData":[OD(0.0)],"derivedFrom":[sQuery(id+"F0.wireOp",EDGE,"E4"),subQ0]});Q14=makeQuery(id+"F1.opExtrude","CAP_EDGE",EDGE,{"disambiguationData":[OSD([subQ0]),TDD([makeQuery(id+"F0.imprint","IMPRINT",EDGE,{"disambiguationData":[TD([[makeQuery(id+"F0.imprint","INTERSECT",VERTEX,{"disambiguationData":[OD(0.0)],"derivedFrom":[sQuery(id+"F0.wireOp",EDGE,"E3"),subQ0]}),-1.0]])],"derivedFrom":subQ0}),makeQuery(id+"F0.imprint","IMPRINT",EDGE,{"disambiguationData":[TD([[subQ1,-1.0]])],"derivedFrom":subQ0})])],"isStart":true});}
            var Q15;
            {var subQ0=sQuery(id+"F0.wireOp",EDGE,"E17");var subQ1=makeQuery(id+"F0.imprint","INTERSECT",VERTEX,{"disambiguationData":[OD(1.0)],"derivedFrom":[sQuery(id+"F0.wireOp",EDGE,"E4"),subQ0]});Q15=makeQuery(id+"F1.opExtrude","CAP_EDGE",EDGE,{"disambiguationData":[OSD([subQ0]),TDD([makeQuery(id+"F0.imprint","IMPRINT",EDGE,{"disambiguationData":[TD([[makeQuery(id+"F0.imprint","INTERSECT",VERTEX,{"disambiguationData":[OD(1.0)],"derivedFrom":[sQuery(id+"F0.wireOp",EDGE,"E3"),subQ0]}),-1.0]])],"derivedFrom":subQ0}),makeQuery(id+"F0.imprint","IMPRINT",EDGE,{"disambiguationData":[TD([[subQ1,-1.0]])],"derivedFrom":subQ0})])],"isStart":true});}
            var Q16;
            {var subQ0=sQuery(id+"F0.wireOp",EDGE,"E3");Q16=makeQuery(id+"F1.opExtrude","CAP_EDGE",EDGE,{"disambiguationData":[OSD([subQ0]),TDD([makeQuery(id+"F0.imprint","IMPRINT",EDGE,{"disambiguationData":[TD([[makeQuery(id+"F0.imprint","INTERSECT",VERTEX,{"disambiguationData":[OD(1.0)],"derivedFrom":[subQ0,sQuery(id+"F0.wireOp",EDGE,"E16")]}),1.0]])],"derivedFrom":subQ0})])],"isStart":true});}
            var Q17;
            {var subQ0=sQuery(id+"F0.wireOp",EDGE,"E16");var subQ1=makeQuery(id+"F0.imprint","INTERSECT",VERTEX,{"disambiguationData":[OD(1.0)],"derivedFrom":[sQuery(id+"F0.wireOp",EDGE,"E4"),subQ0]});Q17=makeQuery(id+"F1.opExtrude","CAP_EDGE",EDGE,{"disambiguationData":[OSD([subQ0]),TDD([makeQuery(id+"F0.imprint","IMPRINT",EDGE,{"disambiguationData":[TD([[subQ1,1.0]])],"derivedFrom":subQ0}),makeQuery(id+"F0.imprint","IMPRINT",EDGE,{"disambiguationData":[TD([[makeQuery(id+"F0.imprint","INTERSECT",VERTEX,{"disambiguationData":[OD(1.0)],"derivedFrom":[sQuery(id+"F0.wireOp",EDGE,"E3"),subQ0]}),1.0]])],"derivedFrom":subQ0})])],"isStart":true});}
            fillet(context, id + "F4", {"entities" : qUnion([Q0, Q1, Q2, Q3, Q4, Q5, Q6, Q7, Q8, Q9, Q10, Q11, Q12, Q13, Q14, Q15, Q16, Q17]), "radius" : 1 * mm, "tangentPropagation" : true, "allowEdgeOverflow" : false});
        }
    });
